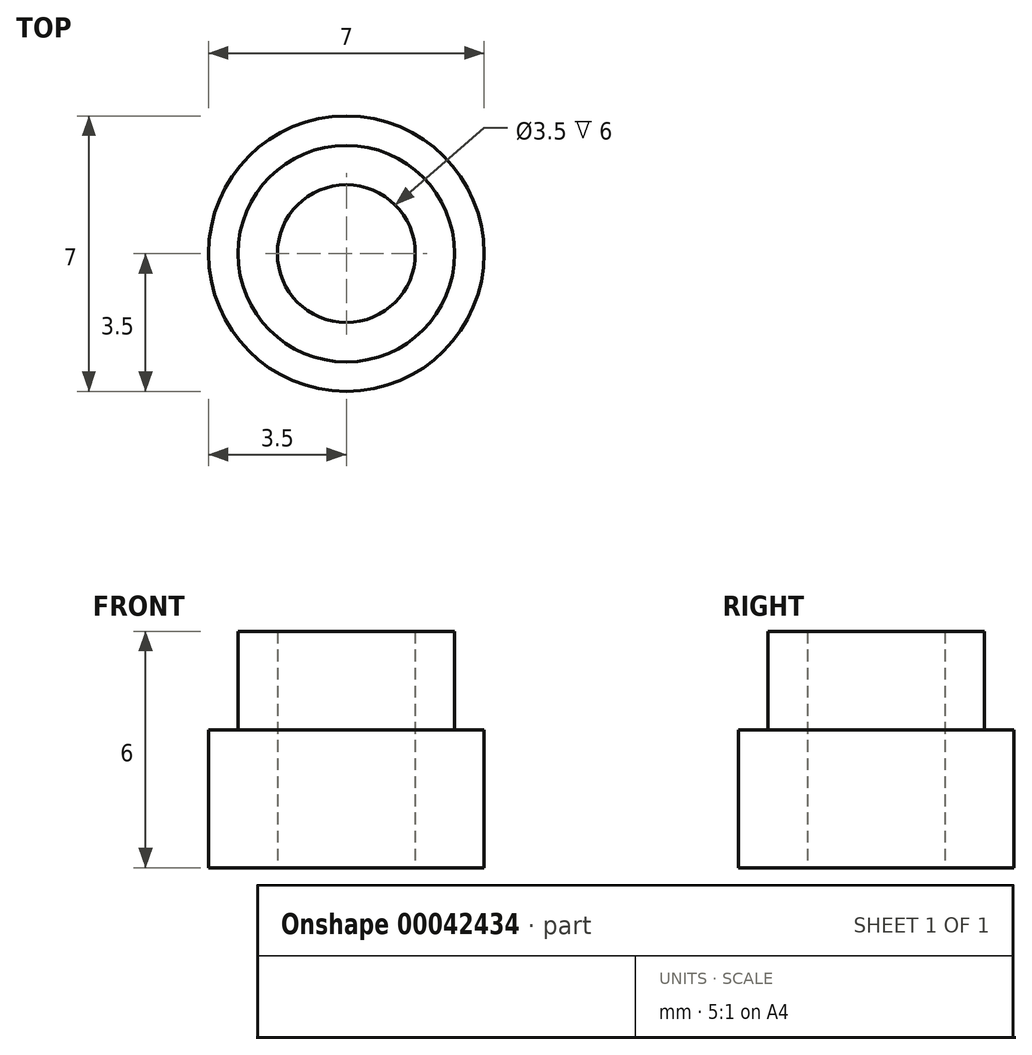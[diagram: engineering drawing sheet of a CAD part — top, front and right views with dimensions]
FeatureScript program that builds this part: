
annotation { "Feature Type Name" : "Feature", "Feature Type Description" : "" }
export const myFeature = defineFeature(function(context is Context, id is Id, definition is map)
    precondition{}
    {
        {
            var Q0;
            Q0=qCreatedBy(makeId("Top.planeOp"),FACE);
            var sketch = newSketch(context, id + "F0", { "sketchPlane" : qUnion([Q0])});
            skCircle(sketch, "E0", {"center": v(0, 0) * mm, "radius": 2.75 * mm});
            skCircle(sketch, "E1", {"center": v(0, 0) * mm, "radius": 1.75 * mm});
            skCircle(sketch, "E2", {"center": v(0, 0) * mm, "radius": 3.5 * mm});
            skLineSegment(sketch, "E3", {"start": v(-7.3, 0) * mm, "end": v(8.92, 0) * mm, "construction": true});
            skSolve(sketch);
        }
        {
            var Q0;
            Q0=makeQuery(id+"F0.imprint","IMPRINT",FACE,{"disambiguationData":[TD([[makeQuery(id+"F0.imprint","IMPRINT",EDGE,{"derivedFrom":sQuery(id+"F0.wireOp",EDGE,"E0")}),1.0]])]});
            extrude(context, id + "F1", {"entities" : qUnion([Q0]), "depth" : 6 * mm});
        }
        {
            var Q0;
            Q0=makeQuery(id+"F0.imprint","IMPRINT",FACE,{"disambiguationData":[TD([[makeQuery(id+"F0.imprint","IMPRINT",EDGE,{"derivedFrom":sQuery(id+"F0.wireOp",EDGE,"E0")}),-1.0]])]});
            var Q1;
            {var subQ0=sQuery(id+"F0.wireOp",EDGE,"5a75ecd3-3456-446d-95bc-d0d0cc41031b.4");var subQ1=sQuery(id+"F0.wireOp",EDGE,"E2");var subQ3=makeQuery(id+"F0.imprint","INTERSECT",VERTEX,{"disambiguationData":[OD(0.0)],"derivedFrom":[subQ1,subQ0]});Q1=makeQuery(id+"F0.imprint","IMPRINT",FACE,{"disambiguationData":[TD([[makeQuery(id+"F0.imprint","IMPRINT",EDGE,{"disambiguationData":[TD([[subQ3,-1.0]])],"derivedFrom":subQ1}),1.0]])]});}
            var Q2;
            {var subQ0=sQuery(id+"F0.wireOp",EDGE,"5a75ecd3-3456-446d-95bc-d0d0cc41031b.3");var subQ1=sQuery(id+"F0.wireOp",EDGE,"E2");var subQ3=makeQuery(id+"F0.imprint","INTERSECT",VERTEX,{"disambiguationData":[OD(0.0)],"derivedFrom":[subQ1,subQ0]});Q2=makeQuery(id+"F0.imprint","IMPRINT",FACE,{"disambiguationData":[TD([[makeQuery(id+"F0.imprint","IMPRINT",EDGE,{"disambiguationData":[TD([[subQ3,-1.0]])],"derivedFrom":subQ1}),1.0]])]});}
            var Q3;
            {var subQ0=sQuery(id+"F0.wireOp",EDGE,"5a75ecd3-3456-446d-95bc-d0d0cc41031b.2");var subQ1=sQuery(id+"F0.wireOp",EDGE,"E2");var subQ3=makeQuery(id+"F0.imprint","INTERSECT",VERTEX,{"disambiguationData":[OD(0.0)],"derivedFrom":[subQ1,subQ0]});Q3=makeQuery(id+"F0.imprint","IMPRINT",FACE,{"disambiguationData":[TD([[makeQuery(id+"F0.imprint","IMPRINT",EDGE,{"disambiguationData":[TD([[subQ3,-1.0]])],"derivedFrom":subQ1}),1.0]])]});}
            var Q4;
            {var subQ0=sQuery(id+"F0.wireOp",EDGE,"5a75ecd3-3456-446d-95bc-d0d0cc41031b.1");var subQ1=sQuery(id+"F0.wireOp",EDGE,"E2");var subQ3=makeQuery(id+"F0.imprint","INTERSECT",VERTEX,{"disambiguationData":[OD(0.0)],"derivedFrom":[subQ1,subQ0]});Q4=makeQuery(id+"F0.imprint","IMPRINT",FACE,{"disambiguationData":[TD([[makeQuery(id+"F0.imprint","IMPRINT",EDGE,{"disambiguationData":[TD([[subQ3,-1.0]])],"derivedFrom":subQ1}),1.0]])]});}
            var Q5;
            {var subQ0=sQuery(id+"F0.wireOp",EDGE,"5a75ecd3-3456-446d-95bc-d0d0cc41031b.0");var subQ1=sQuery(id+"F0.wireOp",EDGE,"E2");var subQ3=makeQuery(id+"F0.imprint","INTERSECT",VERTEX,{"disambiguationData":[OD(0.0)],"derivedFrom":[subQ1,subQ0]});Q5=makeQuery(id+"F0.imprint","IMPRINT",FACE,{"disambiguationData":[TD([[makeQuery(id+"F0.imprint","IMPRINT",EDGE,{"disambiguationData":[TD([[subQ3,-1.0]])],"derivedFrom":subQ1}),1.0]])]});}
            var Q6;
            {var subQ0=sQuery(id+"F0.wireOp",EDGE,"5a75ecd3-3456-446d-95bc-d0d0cc41031b.5");var subQ1=sQuery(id+"F0.wireOp",EDGE,"E2");var subQ3=makeQuery(id+"F0.imprint","INTERSECT",VERTEX,{"disambiguationData":[OD(0.0)],"derivedFrom":[subQ1,subQ0]});Q6=makeQuery(id+"F0.imprint","IMPRINT",FACE,{"disambiguationData":[TD([[makeQuery(id+"F0.imprint","IMPRINT",EDGE,{"disambiguationData":[TD([[subQ3,1.0]])],"derivedFrom":subQ1}),1.0]])]});}
            extrude(context, id + "F2", {"entities" : qUnion([Q0, Q1, Q2, Q3, Q4, Q5, Q6]), "operationType" : NewBodyOperationType.ADD, "depth" : 3.5 * mm});
        }
        {
            var Q0;
            Q0=sQuery(id+"F0.wireOp",EDGE,"E3");
            cPlane(context, id + "F3", {"entities" : qUnion([Q0]), "cplaneType" : CPlaneType.LINE_ANGLE, "offset" : 150 * mm, "angle" : 180 * degree, "width" : 150 * mm, "height" : 150 * mm});
        }
    });
